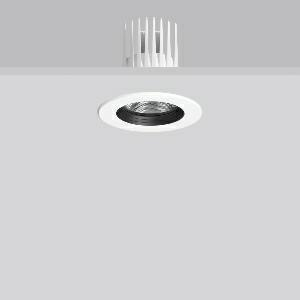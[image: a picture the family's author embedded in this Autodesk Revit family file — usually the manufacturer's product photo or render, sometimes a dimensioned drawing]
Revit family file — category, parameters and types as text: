
# Revit family: heledon_mini_e_901741_002_1_921c
name_source: partatom
category: Lighting Fixtures
units: mm (PartAtom-declared; Revit-internal decimal feet)

## family parameters
Cut with Voids When Loaded = No
Host = Face
Light Source = No
Part Type = Normal
Room Calculation Point = No
Round Connector Dimension = Use Diameter
Shared = No

## types (1)
- HELEDON mini E (1 x LED Modul 940, 2600 lm, 4000)
    Apparent Load = 20 VA
    Approval mark = CE
    CIE Flux Codes = 99 100 100 100 100
    Color Rendering = 92
    Color Temperature = 4000
    Default Elevation = 1800 mm
    Description = Series: HELEDON mini
Round recessed downlight. Housing: die-cast aluminium, powder-coated. Black plastic ring and recessed LED to prevent glare from the side. Optical assembly with reflector made of MIRO-Silver with 98% total light reflection for outstanding efficiency - can be changed without tools. Best colour rendering index Ra>90. Suitable for Recessed ceiling mounting. Installation without tools thanks to spring fastening system. Including separate LED converter with connecting cable 600 mm.High quality converter without flickering and stroboscopic effect. Through-wiring box (5 pole) available as accessory. The following accessories can be mounted without use of tools: interchangeable lenses, decorative glasses, honeycomb louvre, clear and frosted diffusers, white interchangeable plastic ring. 
Colour: traffic white, matt (RAL 9016)
Diameter: 124 mm
Height: 3 mm
Cut-out diameter: 114 mm
Recess height: 170 mm
Luminaire: recess height: 120 mm
Lamp: LED
Socket: without socket
Colour temperature: 4000K
Colour rendering index (CRI): 92
System power: 20 W
Rated luminous flux: 2600 lm
Luminous efficiency: 130 lm/W
Control gear: Regulated power supply
Protection class: II
Type of protection: IP 20
    Height = 0 mm  [stored 0 ft]
    Lamp = 1 x LED Modul 940
    Lamp Light Flux = 2600 lm
    Lamp count = 1
    Length = 124 mm  [stored 0.406824 ft]
    Lifetime = 50000 h
    Luminous efficacy = 130 lm/W
    Manufacturer = RZB
    ModVariant = No
    Model = 901741.002.1
    Mounting Place = Ceiling
    Mounting Type = Recessed
    Number of Poles = 1
    OnlyDefault = Yes
    Power Factor = 1
    Product Name = HELEDON mini E
    Product group = Recessed downlights
    ProductGroupID = 402
    Protection Class = Protection class II
    Protection Degree = IP 20
    RLX_Detail_Level = 1
    RLX_Emergency_Light_Flux = 0 lm
    RLX_Emergency_Type = 0
    RLX_Emergency_Type_DB = No
    RlxData = <blob elided: 124553 chars, md5=9c603b71>
    Socket = socket
    Standby Power = 0 W
    System Light Flux = 2600 lm
    System Power = 20 W
    Type Comments = Product without accessories
    Type Image = 901657.002.jpg
    URL = http://relux.com
    VarID = ---
    Voltage = 230 V
    Voltage Range = 220-240 V
    Weight = 0.00 kg
    Width = 0 mm  [stored 0 ft]

note: [stored X ft] marks values corroborated as IEEE doubles in the binary element streams (Revit-internal decimal feet)

## geometry (parser evidence)
native form markers: Blend x4, Sweep x11
no freeform markers — native parametric forms only
